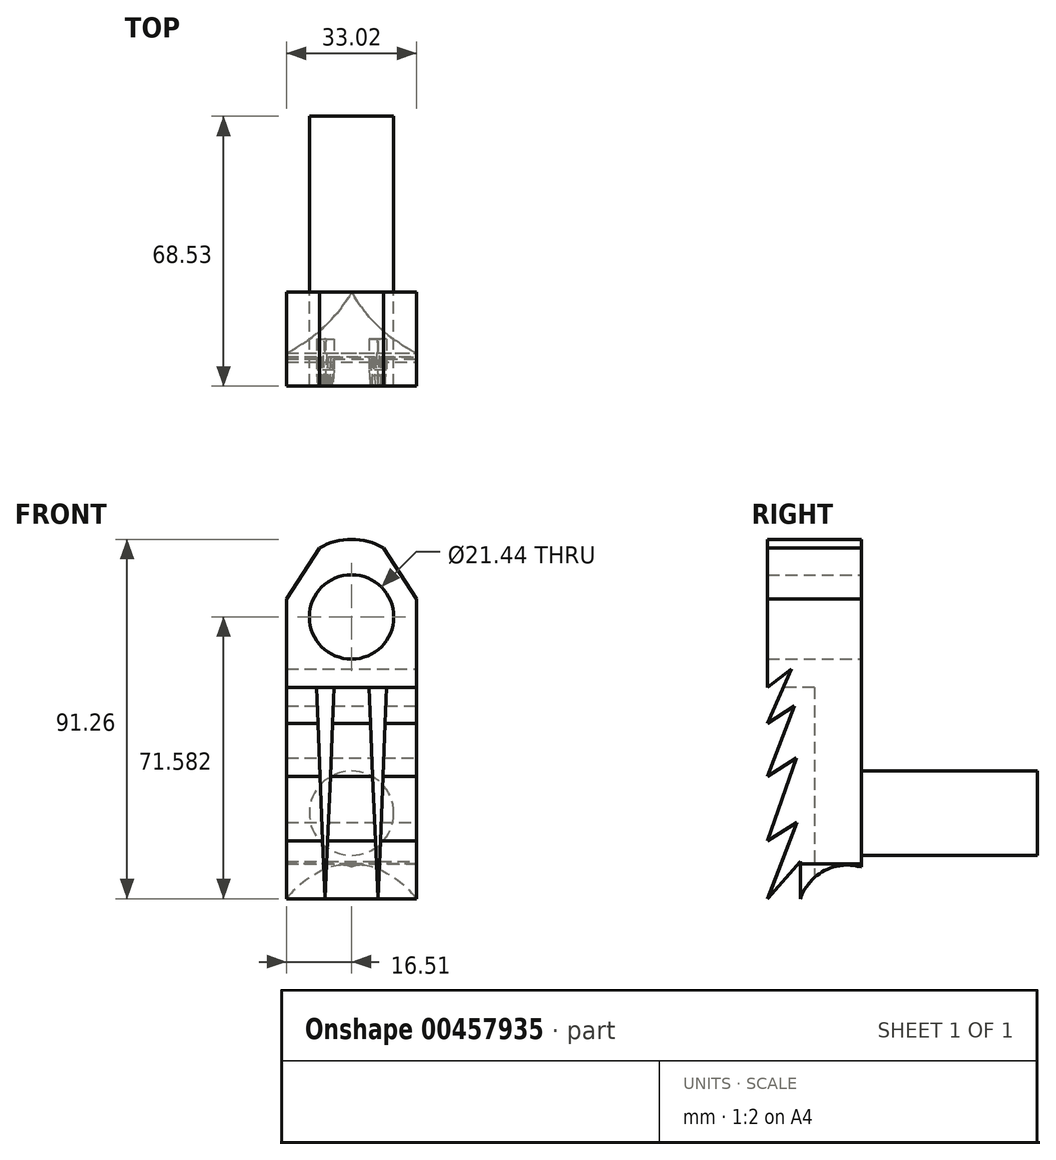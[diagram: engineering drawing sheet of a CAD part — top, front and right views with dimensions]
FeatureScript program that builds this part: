
annotation { "Feature Type Name" : "Feature", "Feature Type Description" : "" }
export const myFeature = defineFeature(function(context is Context, id is Id, definition is map)
    precondition{}
    {
        {
            var Q0;
            Q0=qCreatedBy(makeId("Front.planeOp"),FACE);
            var sketch = newSketch(context, id + "F0", { "sketchPlane" : qUnion([Q0])});
            skLineSegment(sketch, "E0.bottom", {"start": v(-16.51, 50.8) * mm, "end": v(16.51, 50.8) * mm});
            skLineSegment(sketch, "E0.top", {"start": v(-16.51, -50.8) * mm, "end": v(16.51, -50.8) * mm});
            skLineSegment(sketch, "E0.left", {"start": v(-16.51, 50.8) * mm, "end": v(-16.51, -50.8) * mm});
            skLineSegment(sketch, "E0.right", {"start": v(16.51, 50.8) * mm, "end": v(16.51, -50.8) * mm});
            skPoint(sketch, "E0.middle", {"position": v(0, 0) * mm});
            skLineSegment(sketch, "E1", {"start": v(0, 50.8) * mm, "end": v(0, -50.8) * mm});
            skLineSegment(sketch, "E2", {"start": v(-16.51, 0) * mm, "end": v(16.51, 0) * mm});
            skPoint(sketch, "E3", {"position": v(0, 20.78) * mm});
            skCircle(sketch, "E4", {"center": v(0, 20.78) * mm, "radius": 10.72 * mm});
            skPoint(sketch, "E5", {"position": v(0, -29.08) * mm});
            skCircle(sketch, "E6", {"center": v(0, -29.08) * mm, "radius": 10.72 * mm});
            skPoint(sketch, "E7", {"position": v(-16.51, 25.4) * mm});
            skPoint(sketch, "E8", {"position": v(16.51, 25.4) * mm});
            skLineSegment(sketch, "E9", {"start": v(-16.51, 25.4) * mm, "end": v(0, 50.8) * mm});
            skLineSegment(sketch, "E10", {"start": v(16.51, 25.4) * mm, "end": v(0, 50.8) * mm});
            skArc(sketch, "E11", {"start": v(16.51, 25.4) * mm, "mid": v(0, 40.46) * mm, "end": v(-16.51, 25.4) * mm});
            skSolve(sketch);
        }
        {
            var Q0;
            {var subQ1=sQuery(id+"F0.wireOp",EDGE,"E0.top");var subQ5=sQuery(id+"F0.wireOp",EDGE,"E0.right");var subQ6=makeQuery(id+"F0.imprint","INTERSECT",VERTEX,{"derivedFrom":[subQ1,subQ5]});Q0=makeQuery(id+"F0.imprint","IMPRINT",FACE,{"disambiguationData":[TD([[makeQuery(id+"F0.imprint","IMPRINT",EDGE,{"disambiguationData":[TD([[subQ6,1.0]])],"derivedFrom":subQ1}),1.0]])]});}
            var Q1;
            {var subQ1=sQuery(id+"F0.wireOp",EDGE,"E0.top");var subQ8=sQuery(id+"F0.wireOp",EDGE,"E0.left");var subQ9=makeQuery(id+"F0.imprint","INTERSECT",VERTEX,{"derivedFrom":[subQ1,subQ8]});Q1=makeQuery(id+"F0.imprint","IMPRINT",FACE,{"disambiguationData":[TD([[makeQuery(id+"F0.imprint","IMPRINT",EDGE,{"disambiguationData":[TD([[subQ9,-1.0]])],"derivedFrom":subQ1}),1.0]])]});}
            var Q2;
            {var subQ0=sQuery(id+"F0.wireOp",EDGE,"E6");var subQ1=sQuery(id+"F0.wireOp",EDGE,"E1");var subQ2=makeQuery(id+"F0.imprint","INTERSECT",VERTEX,{"disambiguationData":[OD(0.0)],"derivedFrom":[subQ1,subQ0]});Q2=makeQuery(id+"F0.imprint","IMPRINT",FACE,{"disambiguationData":[TD([[makeQuery(id+"F0.imprint","IMPRINT",EDGE,{"disambiguationData":[TD([[subQ2,-1.0]])],"derivedFrom":subQ1}),-1.0]])]});}
            var Q3;
            {var subQ0=sQuery(id+"F0.wireOp",EDGE,"E6");var subQ1=sQuery(id+"F0.wireOp",EDGE,"E1");var subQ2=makeQuery(id+"F0.imprint","INTERSECT",VERTEX,{"disambiguationData":[OD(0.0)],"derivedFrom":[subQ1,subQ0]});Q3=makeQuery(id+"F0.imprint","IMPRINT",FACE,{"disambiguationData":[TD([[makeQuery(id+"F0.imprint","IMPRINT",EDGE,{"disambiguationData":[TD([[subQ2,-1.0]])],"derivedFrom":subQ1}),1.0]])]});}
            var Q4;
            {var subQ0=sQuery(id+"F0.wireOp",EDGE,"E11");var subQ1=sQuery(id+"F0.wireOp",EDGE,"E1");var subQ2=makeQuery(id+"F0.imprint","INTERSECT",VERTEX,{"derivedFrom":[subQ1,subQ0]});Q4=makeQuery(id+"F0.imprint","IMPRINT",FACE,{"disambiguationData":[TD([[makeQuery(id+"F0.imprint","IMPRINT",EDGE,{"disambiguationData":[TD([[subQ2,-1.0]])],"derivedFrom":subQ1}),1.0]])]});}
            var Q5;
            {var subQ3=sQuery(id+"F0.wireOp",EDGE,"E1");var subQ7=sQuery(id+"F0.wireOp",EDGE,"E11");var subQ8=makeQuery(id+"F0.imprint","INTERSECT",VERTEX,{"derivedFrom":[subQ3,subQ7]});Q5=makeQuery(id+"F0.imprint","IMPRINT",FACE,{"disambiguationData":[TD([[makeQuery(id+"F0.imprint","IMPRINT",EDGE,{"disambiguationData":[TD([[subQ8,-1.0]])],"derivedFrom":subQ3}),-1.0]])]});}
            extrude(context, id + "F1", {"entities" : qUnion([Q0, Q1, Q2, Q3, Q4, Q5]), "depth" : 49.23 * mm, "offsetDistance" : 25.4 * mm});
        }
        {
            var Q0;
            {var subQ0=sQuery(id+"F0.wireOp",EDGE,"E6");var subQ1=sQuery(id+"F0.wireOp",EDGE,"E1");var subQ2=makeQuery(id+"F0.imprint","INTERSECT",VERTEX,{"disambiguationData":[OD(0.0)],"derivedFrom":[subQ1,subQ0]});Q0=makeQuery(id+"F0.imprint","IMPRINT",FACE,{"disambiguationData":[TD([[makeQuery(id+"F0.imprint","IMPRINT",EDGE,{"disambiguationData":[TD([[subQ2,-1.0]])],"derivedFrom":subQ1}),1.0]])]});}
            var Q1;
            {var subQ0=sQuery(id+"F0.wireOp",EDGE,"E6");var subQ1=sQuery(id+"F0.wireOp",EDGE,"E1");var subQ2=makeQuery(id+"F0.imprint","INTERSECT",VERTEX,{"disambiguationData":[OD(0.0)],"derivedFrom":[subQ1,subQ0]});Q1=makeQuery(id+"F0.imprint","IMPRINT",FACE,{"disambiguationData":[TD([[makeQuery(id+"F0.imprint","IMPRINT",EDGE,{"disambiguationData":[TD([[subQ2,-1.0]])],"derivedFrom":subQ1}),-1.0]])]});}
            extrude(context, id + "F2", {"entities" : qUnion([Q0, Q1]), "operationType" : NewBodyOperationType.ADD, "oppositeDirection" : true, "depth" : 19.3 * mm, "offsetDistance" : 25.4 * mm});
        }
        {
            var Q0;
            Q0=makeQuery(id+"F1.opExtrude","CAP_FACE",FACE,{"disambiguationData":[OSD([sQuery(id+"F0.wireOp",EDGE,"E0.top"),sQuery(id+"F0.wireOp",EDGE,"E0.left"),sQuery(id+"F0.wireOp",EDGE,"E0.right"),sQuery(id+"F0.wireOp",EDGE,"E4"),sQuery(id+"F0.wireOp",EDGE,"E9"),sQuery(id+"F0.wireOp",EDGE,"E10"),sQuery(id+"F0.wireOp",EDGE,"E11")])],"isStart":true});
            extrude(context, id + "F3", {"entities" : qUnion([Q0]), "operationType" : NewBodyOperationType.REMOVE, "oppositeDirection" : true, "depth" : 25.4 * mm, "offsetDistance" : 25.4 * mm});
        }
        {
            var Q0;
            Q0=makeQuery(id+"F1.opExtrude","SWEPT_FACE",FACE,{"disambiguationData":[OSD([sQuery(id+"F0.wireOp",EDGE,"E0.right")])]});
            var sketch = newSketch(context, id + "F4", { "sketchPlane" : qUnion([Q0])});
            skLineSegment(sketch, "E12", {"start": v(-49.23, -50.8) * mm, "end": v(-41.71, -31.47) * mm});
            skLineSegment(sketch, "E13", {"start": v(-41.71, -31.47) * mm, "end": v(-49.23, -36.16) * mm});
            skLineSegment(sketch, "E14", {"start": v(-49.23, -36.16) * mm, "end": v(-41.93, -15.04) * mm});
            skLineSegment(sketch, "E15", {"start": v(-41.93, -15.04) * mm, "end": v(-49.23, -19.74) * mm});
            skLineSegment(sketch, "E16", {"start": v(-49.23, -19.74) * mm, "end": v(-42.35, -1.81) * mm});
            skLineSegment(sketch, "E17", {"start": v(-42.35, -1.81) * mm, "end": v(-49.23, -6.3) * mm});
            skLineSegment(sketch, "E18", {"start": v(-49.23, -6.3) * mm, "end": v(-43.2, 7.57) * mm});
            skLineSegment(sketch, "E19", {"start": v(-43.2, 7.57) * mm, "end": v(-49.23, 2.88) * mm});
            skLineSegment(sketch, "E20", {"start": v(-49.23, -50.8) * mm, "end": v(-40.87, -41.29) * mm});
            skLineSegment(sketch, "E21", {"start": v(-40.87, -41.29) * mm, "end": v(-40.87, -50.8) * mm});
            skSolve(sketch);
        }
        {
            var Q0;
            {var subQ0=sQuery(id+"F4.wireOp",EDGE,"E18");Q0=makeQuery(id+"F4.imprint","IMPRINT",FACE,{"disambiguationData":[TD([[makeQuery(id+"F4.imprint","IMPRINT",EDGE,{"derivedFrom":subQ0}),1.0]])]});}
            var Q1;
            {var subQ0=sQuery(id+"F4.wireOp",EDGE,"E16");Q1=makeQuery(id+"F4.imprint","IMPRINT",FACE,{"disambiguationData":[TD([[makeQuery(id+"F4.imprint","IMPRINT",EDGE,{"derivedFrom":subQ0}),1.0]])]});}
            var Q2;
            {var subQ0=sQuery(id+"F4.wireOp",EDGE,"E14");Q2=makeQuery(id+"F4.imprint","IMPRINT",FACE,{"disambiguationData":[TD([[makeQuery(id+"F4.imprint","IMPRINT",EDGE,{"derivedFrom":subQ0}),1.0]])]});}
            var Q3;
            {var subQ0=sQuery(id+"F4.wireOp",EDGE,"E12");Q3=makeQuery(id+"F4.imprint","IMPRINT",FACE,{"disambiguationData":[TD([[makeQuery(id+"F4.imprint","IMPRINT",EDGE,{"derivedFrom":subQ0}),1.0]])]});}
            var Q4;
            {var subQ0=sQuery(id+"F4.wireOp",EDGE,"E20");Q4=makeQuery(id+"F4.imprint","IMPRINT",FACE,{"disambiguationData":[TD([[makeQuery(id+"F4.imprint","IMPRINT",EDGE,{"derivedFrom":subQ0}),-1.0]])]});}
            extrude(context, id + "F5", {"entities" : qUnion([Q0, Q1, Q2, Q3, Q4]), "operationType" : NewBodyOperationType.REMOVE, "oppositeDirection" : true, "depth" : 52.83 * mm, "offsetDistance" : 25.4 * mm});
        }
        {
            var Q0;
            Q0=makeQuery(id+"F1.opExtrude","CAP_FACE",FACE,{"disambiguationData":[OSD([sQuery(id+"F0.wireOp",EDGE,"E0.top"),sQuery(id+"F0.wireOp",EDGE,"E0.left"),sQuery(id+"F0.wireOp",EDGE,"E0.right"),sQuery(id+"F0.wireOp",EDGE,"E4"),sQuery(id+"F0.wireOp",EDGE,"E9"),sQuery(id+"F0.wireOp",EDGE,"E10"),sQuery(id+"F0.wireOp",EDGE,"E11")])],"isStart":false});
            var sketch = newSketch(context, id + "F6", { "sketchPlane" : qUnion([Q0])});
            skLineSegment(sketch, "E22", {"start": v(-8.87, 2.88) * mm, "end": v(-6.74, -50.67) * mm});
            skLineSegment(sketch, "E23", {"start": v(-6.74, -50.67) * mm, "end": v(-4.39, 2.88) * mm});
            skLineSegment(sketch, "E24.MirrorCS", {"start": v(8.87, 2.88) * mm, "end": v(6.74, -50.67) * mm});
            skLineSegment(sketch, "E25.MirrorCS", {"start": v(6.74, -50.67) * mm, "end": v(4.39, 2.88) * mm});
            skSolve(sketch);
        }
        {
            var Q0;
            {var subQ0=sQuery(id+"F6.wireOp",EDGE,"E22");Q0=makeQuery(id+"F6.imprint","IMPRINT",FACE,{"disambiguationData":[TD([[makeQuery(id+"F6.imprint","IMPRINT",EDGE,{"derivedFrom":subQ0}),1.0]])]});}
            var Q1;
            {var subQ0=sQuery(id+"F6.wireOp",EDGE,"E24.MirrorCS");Q1=makeQuery(id+"F6.imprint","IMPRINT",FACE,{"disambiguationData":[TD([[makeQuery(id+"F6.imprint","IMPRINT",EDGE,{"derivedFrom":subQ0}),-1.0]])]});}
            extrude(context, id + "F7", {"entities" : qUnion([Q0, Q1]), "operationType" : NewBodyOperationType.REMOVE, "oppositeDirection" : true, "depth" : 11.94 * mm, "offsetDistance" : 25.4 * mm});
        }
        {
            var Q0;
            Q0=makeQuery(id+"F1.opExtrude","SWEPT_FACE",FACE,{"disambiguationData":[OSD([sQuery(id+"F0.wireOp",EDGE,"E0.left")])]});
            var sketch = newSketch(context, id + "F8", { "sketchPlane" : qUnion([Q0])});
            skArc(sketch, "E26", {"start": v(40.87, -50.8) * mm, "mid": v(34.75, -43.68) * mm, "end": v(25.4, -42.78) * mm});
            skSolve(sketch);
        }
        {
            var Q0;
            {var subQ0=sQuery(id+"F8.wireOp",EDGE,"E26");Q0=makeQuery(id+"F8.imprint","IMPRINT",FACE,{"disambiguationData":[TD([[makeQuery(id+"F8.imprint","IMPRINT",EDGE,{"derivedFrom":subQ0}),1.0]])]});}
            extrude(context, id + "F9", {"entities" : qUnion([Q0]), "operationType" : NewBodyOperationType.REMOVE, "oppositeDirection" : true, "depth" : 122.94 * mm, "offsetDistance" : 25.4 * mm});
        }
        {
            var Q0;
            Q0=makeQuery(id+"F9.boolean.opBoolean","COPY",FACE,{"derivedFrom":makeQuery(id+"F9.opExtrude","SWEPT_FACE",FACE,{"disambiguationData":[OSD([sQuery(id+"F8.wireOp",EDGE,"E26")])]})});
            cPlane(context, id + "F10", {"entities" : qUnion([Q0]), "cplaneType" : CPlaneType.LINE_ANGLE, "offset" : 25.4 * mm, "angle" : 90 * degree, "width" : 152.4 * mm, "height" : 152.4 * mm});
        }
        {
            var Q0;
            Q0=qCreatedBy(id+"F10.planeOp",FACE);
            var sketch = newSketch(context, id + "F11", { "sketchPlane" : qUnion([Q0])});
            skLineSegment(sketch, "E27.0", {"start": v(-16.51, -40.87) * mm, "end": v(-16.51, -25.4) * mm});
            skLineSegment(sketch, "E28.0", {"start": v(16.51, -25.4) * mm, "end": v(16.51, -40.87) * mm});
            skPoint(sketch, "E29.0", {"position": v(0, -49.23) * mm});
            skPoint(sketch, "E30.0", {"position": v(0, -25.4) * mm});
            skArc(sketch, "E31", {"start": v(-16.51, -40.87) * mm, "mid": v(-7.1, -34.38) * mm, "end": v(0, -25.4) * mm});
            skArc(sketch, "E32", {"start": v(0, -25.4) * mm, "mid": v(7.1, -34.38) * mm, "end": v(16.51, -40.87) * mm});
            skLineSegment(sketch, "E33.0", {"start": v(16.51, -25.4) * mm, "end": v(-16.5, -25.4) * mm});
            skSolve(sketch);
        }
        {
            var Q0;
            {var subQ0=sQuery(id+"F11.wireOp",EDGE,"E27.0");Q0=makeQuery(id+"F11.imprint","IMPRINT",FACE,{"disambiguationData":[TD([[makeQuery(id+"F11.imprint","IMPRINT",EDGE,{"derivedFrom":subQ0}),-1.0]])]});}
            var Q1;
            {var subQ0=sQuery(id+"F11.wireOp",EDGE,"E28.0");Q1=makeQuery(id+"F11.imprint","IMPRINT",FACE,{"disambiguationData":[TD([[makeQuery(id+"F11.imprint","IMPRINT",EDGE,{"derivedFrom":subQ0}),-1.0]])]});}
            extrude(context, id + "F12", {"entities" : qUnion([Q0, Q1]), "operationType" : NewBodyOperationType.REMOVE, "depth" : 12.95 * mm, "offsetDistance" : 25.4 * mm});
        }
    });
